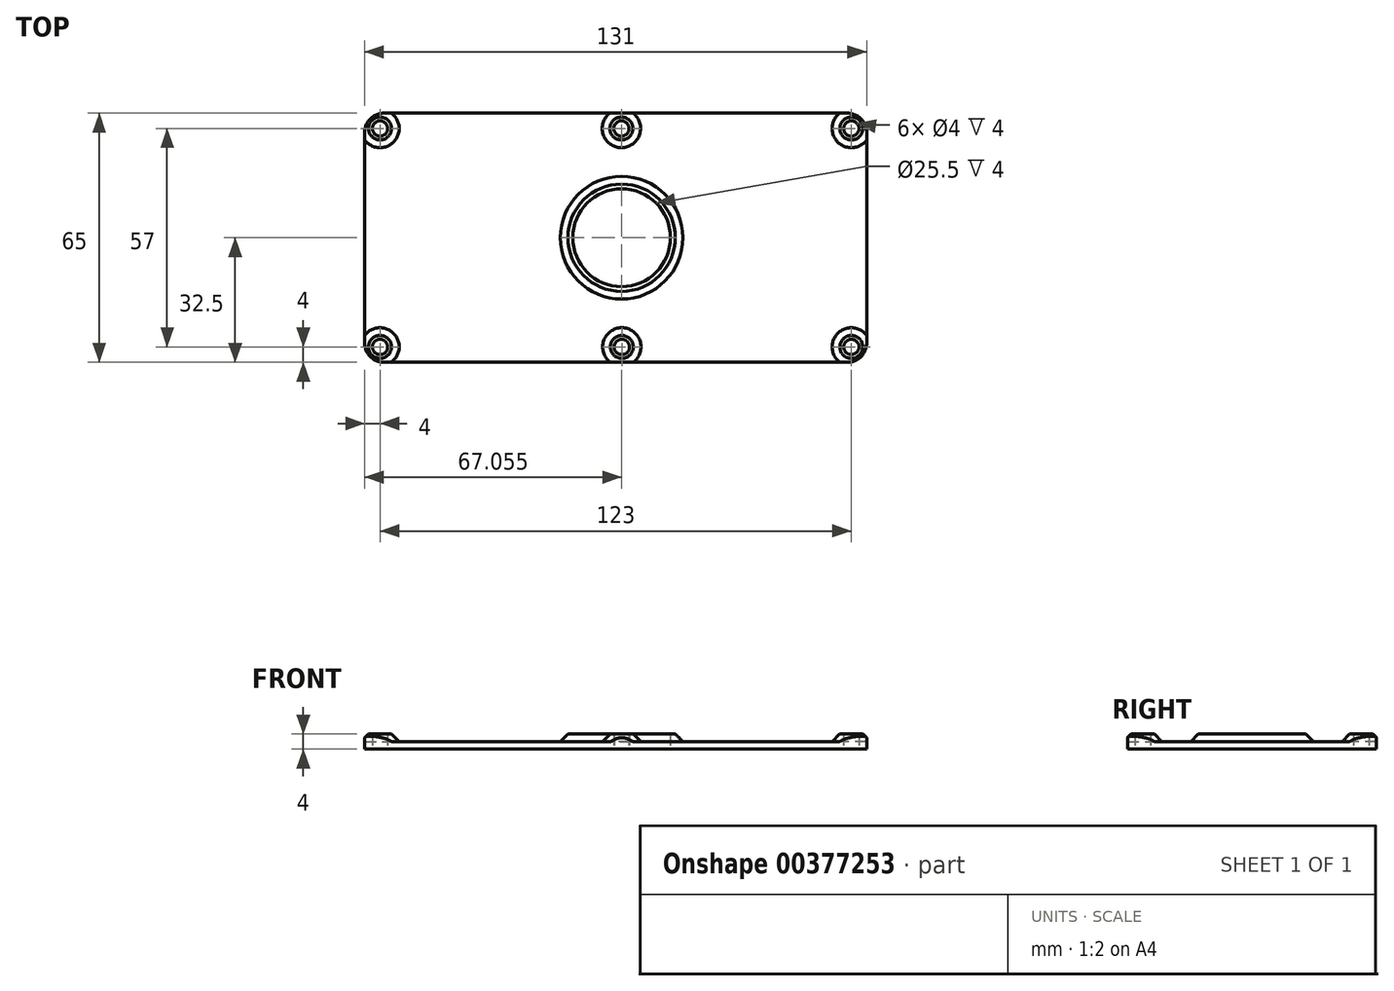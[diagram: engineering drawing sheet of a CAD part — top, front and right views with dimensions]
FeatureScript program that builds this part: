
annotation { "Feature Type Name" : "Feature", "Feature Type Description" : "" }
export const myFeature = defineFeature(function(context is Context, id is Id, definition is map)
    precondition{}
    {
        {
            var Q0;
            Q0=qCreatedBy(makeId("Top.planeOp"),FACE);
            var sketch = newSketch(context, id + "F0", { "sketchPlane" : qUnion([Q0])});
            skLineSegment(sketch, "E0.bottom", {"start": v(-65.5, 32.5) * mm, "end": v(65.5, 32.5) * mm});
            skLineSegment(sketch, "E0.top", {"start": v(-65.5, -32.5) * mm, "end": v(65.5, -32.5) * mm});
            skLineSegment(sketch, "E0.left", {"start": v(-65.5, 32.5) * mm, "end": v(-65.5, -32.5) * mm});
            skLineSegment(sketch, "E0.right", {"start": v(65.5, 32.5) * mm, "end": v(65.5, -32.5) * mm});
            skPoint(sketch, "E0.middle", {"position": v(0, 0) * mm});
            skLineSegment(sketch, "E1.bottom", {"start": v(-65.5, 32.5) * mm, "end": v(-61.5, 32.5) * mm, "construction": true});
            skLineSegment(sketch, "E1.top", {"start": v(-65.5, 28.5) * mm, "end": v(-61.5, 28.5) * mm, "construction": true});
            skLineSegment(sketch, "E1.left", {"start": v(-65.5, 32.5) * mm, "end": v(-65.5, 28.5) * mm, "construction": true});
            skLineSegment(sketch, "E1.right", {"start": v(-61.5, 32.5) * mm, "end": v(-61.5, 28.5) * mm, "construction": true});
            skLineSegment(sketch, "E2.bottom", {"start": v(65.5, 32.5) * mm, "end": v(61.5, 32.5) * mm, "construction": true});
            skLineSegment(sketch, "E2.top", {"start": v(65.5, 28.5) * mm, "end": v(61.5, 28.5) * mm, "construction": true});
            skLineSegment(sketch, "E2.left", {"start": v(65.5, 32.5) * mm, "end": v(65.5, 28.5) * mm, "construction": true});
            skLineSegment(sketch, "E2.right", {"start": v(61.5, 32.5) * mm, "end": v(61.5, 28.5) * mm, "construction": true});
            skLineSegment(sketch, "E3.bottom", {"start": v(-65.5, -32.5) * mm, "end": v(-61.5, -32.5) * mm, "construction": true});
            skLineSegment(sketch, "E3.top", {"start": v(-65.5, -28.5) * mm, "end": v(-61.5, -28.5) * mm, "construction": true});
            skLineSegment(sketch, "E3.left", {"start": v(-65.5, -32.5) * mm, "end": v(-65.5, -28.5) * mm, "construction": true});
            skLineSegment(sketch, "E3.right", {"start": v(-61.5, -32.5) * mm, "end": v(-61.5, -28.5) * mm, "construction": true});
            skLineSegment(sketch, "E4.bottom", {"start": v(65.5, -32.5) * mm, "end": v(61.5, -32.5) * mm, "construction": true});
            skLineSegment(sketch, "E4.top", {"start": v(65.5, -28.5) * mm, "end": v(61.5, -28.5) * mm, "construction": true});
            skLineSegment(sketch, "E4.left", {"start": v(65.5, -32.5) * mm, "end": v(65.5, -28.5) * mm, "construction": true});
            skLineSegment(sketch, "E4.right", {"start": v(61.5, -32.5) * mm, "end": v(61.5, -28.5) * mm, "construction": true});
            skCircle(sketch, "E5", {"center": v(-61.5, 28.5) * mm, "radius": 3 * mm});
            skCircle(sketch, "E6", {"center": v(-61.5, -28.5) * mm, "radius": 3 * mm});
            skCircle(sketch, "E7", {"center": v(61.5, -28.5) * mm, "radius": 3 * mm});
            skCircle(sketch, "E8", {"center": v(61.5, 28.5) * mm, "radius": 3 * mm});
            skLineSegment(sketch, "E9", {"start": v(65.5, 28.5) * mm, "end": v(1.5, 28.5) * mm, "construction": true});
            skPoint(sketch, "E9.endSnap0", {"position": v(63.5, 28.5) * mm});
            skLineSegment(sketch, "E10", {"start": v(65.5, -28.5) * mm, "end": v(1.61, -28.5) * mm});
            skLineSegment(sketch, "E11", {"start": v(1.5, 28.5) * mm, "end": v(1.5, 32.5) * mm, "construction": true});
            skLineSegment(sketch, "E12", {"start": v(1.61, -28.5) * mm, "end": v(1.61, -32.5) * mm, "construction": true});
            skCircle(sketch, "E13", {"center": v(1.5, 28.5) * mm, "radius": 3 * mm});
            skCircle(sketch, "E14", {"center": v(1.61, -28.5) * mm, "radius": 3 * mm});
            skLineSegment(sketch, "E15", {"start": v(1.5, 28.5) * mm, "end": v(1.61, -29.33) * mm, "construction": true});
            skCircle(sketch, "E16", {"center": v(1.55, 0) * mm, "radius": 14 * mm});
            skCircle(sketch, "E17", {"center": v(1.55, 0) * mm, "radius": 12.75 * mm});
            skSolve(sketch);
        }
        {
            var Q0;
            {var subQ7=sQuery(id+"F0.wireOp",EDGE,"E0.bottom");Q0=makeQuery(id+"F0.imprint","IMPRINT",FACE,{"disambiguationData":[TD([[makeQuery(id+"F0.imprint","IMPRINT",EDGE,{"derivedFrom":subQ7}),-1.0]])]});}
            var Q1;
            Q1=makeQuery(id+"F0.imprint","IMPRINT",FACE,{"disambiguationData":[TD([[makeQuery(id+"F0.imprint","IMPRINT",EDGE,{"derivedFrom":sQuery(id+"F0.wireOp",EDGE,"E13")}),1.0]])]});
            var Q2;
            Q2=makeQuery(id+"F0.imprint","IMPRINT",FACE,{"disambiguationData":[TD([[makeQuery(id+"F0.imprint","IMPRINT",EDGE,{"derivedFrom":sQuery(id+"F0.wireOp",EDGE,"E14")}),1.0]])]});
            var Q3;
            {var subQ0=sQuery(id+"F0.wireOp",EDGE,"E10");var subQ1=sQuery(id+"F0.wireOp",EDGE,"E7");var subQ2=makeQuery(id+"F0.imprint","INTERSECT",VERTEX,{"disambiguationData":[OD(0.0)],"derivedFrom":[subQ1,subQ0]});Q3=makeQuery(id+"F0.imprint","IMPRINT",FACE,{"disambiguationData":[TD([[makeQuery(id+"F0.imprint","IMPRINT",EDGE,{"disambiguationData":[TD([[subQ2,1.0]])],"derivedFrom":subQ1}),1.0]])]});}
            var Q4;
            {var subQ0=sQuery(id+"F0.wireOp",EDGE,"E10");var subQ1=sQuery(id+"F0.wireOp",EDGE,"E7");var subQ2=makeQuery(id+"F0.imprint","INTERSECT",VERTEX,{"disambiguationData":[OD(0.0)],"derivedFrom":[subQ1,subQ0]});Q4=makeQuery(id+"F0.imprint","IMPRINT",FACE,{"disambiguationData":[TD([[makeQuery(id+"F0.imprint","IMPRINT",EDGE,{"disambiguationData":[TD([[subQ2,-1.0]])],"derivedFrom":subQ1}),1.0]])]});}
            var Q5;
            Q5=makeQuery(id+"F0.imprint","IMPRINT",FACE,{"disambiguationData":[TD([[makeQuery(id+"F0.imprint","IMPRINT",EDGE,{"derivedFrom":sQuery(id+"F0.wireOp",EDGE,"E8")}),1.0]])]});
            var Q6;
            Q6=makeQuery(id+"F0.imprint","IMPRINT",FACE,{"disambiguationData":[TD([[makeQuery(id+"F0.imprint","IMPRINT",EDGE,{"derivedFrom":sQuery(id+"F0.wireOp",EDGE,"E6")}),1.0]])]});
            var Q7;
            Q7=makeQuery(id+"F0.imprint","IMPRINT",FACE,{"disambiguationData":[TD([[makeQuery(id+"F0.imprint","IMPRINT",EDGE,{"derivedFrom":sQuery(id+"F0.wireOp",EDGE,"E5")}),1.0]])]});
            var Q8;
            Q8=makeQuery(id+"F0.imprint","IMPRINT",FACE,{"disambiguationData":[TD([[makeQuery(id+"F0.imprint","IMPRINT",EDGE,{"derivedFrom":sQuery(id+"F0.wireOp",EDGE,"E16")}),1.0]])]});
            extrude(context, id + "F1", {"entities" : qUnion([Q0, Q1, Q2, Q3, Q4, Q5, Q6, Q7, Q8]), "depth" : 2 * mm});
        }
        {
            var Q0;
            Q0=makeQuery(id+"F0.imprint","IMPRINT",FACE,{"disambiguationData":[TD([[makeQuery(id+"F0.imprint","IMPRINT",EDGE,{"derivedFrom":sQuery(id+"F0.wireOp",EDGE,"E5")}),1.0]])]});
            var Q1;
            Q1=makeQuery(id+"F0.imprint","IMPRINT",FACE,{"disambiguationData":[TD([[makeQuery(id+"F0.imprint","IMPRINT",EDGE,{"derivedFrom":sQuery(id+"F0.wireOp",EDGE,"E6")}),1.0]])]});
            var Q2;
            Q2=makeQuery(id+"F0.imprint","IMPRINT",FACE,{"disambiguationData":[TD([[makeQuery(id+"F0.imprint","IMPRINT",EDGE,{"derivedFrom":sQuery(id+"F0.wireOp",EDGE,"E14")}),1.0]])]});
            var Q3;
            {var subQ0=sQuery(id+"F0.wireOp",EDGE,"E10");var subQ1=sQuery(id+"F0.wireOp",EDGE,"E7");var subQ2=makeQuery(id+"F0.imprint","INTERSECT",VERTEX,{"disambiguationData":[OD(0.0)],"derivedFrom":[subQ1,subQ0]});Q3=makeQuery(id+"F0.imprint","IMPRINT",FACE,{"disambiguationData":[TD([[makeQuery(id+"F0.imprint","IMPRINT",EDGE,{"disambiguationData":[TD([[subQ2,1.0]])],"derivedFrom":subQ1}),1.0]])]});}
            var Q4;
            {var subQ0=sQuery(id+"F0.wireOp",EDGE,"E10");var subQ1=sQuery(id+"F0.wireOp",EDGE,"E7");var subQ2=makeQuery(id+"F0.imprint","INTERSECT",VERTEX,{"disambiguationData":[OD(0.0)],"derivedFrom":[subQ1,subQ0]});Q4=makeQuery(id+"F0.imprint","IMPRINT",FACE,{"disambiguationData":[TD([[makeQuery(id+"F0.imprint","IMPRINT",EDGE,{"disambiguationData":[TD([[subQ2,-1.0]])],"derivedFrom":subQ1}),1.0]])]});}
            var Q5;
            Q5=makeQuery(id+"F0.imprint","IMPRINT",FACE,{"disambiguationData":[TD([[makeQuery(id+"F0.imprint","IMPRINT",EDGE,{"derivedFrom":sQuery(id+"F0.wireOp",EDGE,"E8")}),1.0]])]});
            var Q6;
            Q6=makeQuery(id+"F0.imprint","IMPRINT",FACE,{"disambiguationData":[TD([[makeQuery(id+"F0.imprint","IMPRINT",EDGE,{"derivedFrom":sQuery(id+"F0.wireOp",EDGE,"E13")}),1.0]])]});
            extrude(context, id + "F2", {"entities" : qUnion([Q0, Q1, Q2, Q3, Q4, Q5, Q6]), "operationType" : NewBodyOperationType.ADD, "depth" : 4 * mm});
        }
        {
            var Q0;
            Q0=makeQuery(id+"F2.opExtrude","CAP_FACE",FACE,{"disambiguationData":[OSD([sQuery(id+"F0.wireOp",EDGE,"E5")])],"isStart":false});
            var Q1;
            Q1=makeQuery(id+"F2.opExtrude","CAP_FACE",FACE,{"disambiguationData":[OSD([sQuery(id+"F0.wireOp",EDGE,"E13")])],"isStart":false});
            var Q2;
            Q2=makeQuery(id+"F2.opExtrude","CAP_FACE",FACE,{"disambiguationData":[OSD([sQuery(id+"F0.wireOp",EDGE,"E8")])],"isStart":false});
            var Q3;
            Q3=makeQuery(id+"F2.opExtrude","CAP_FACE",FACE,{"disambiguationData":[OSD([sQuery(id+"F0.wireOp",EDGE,"E7")])],"isStart":false});
            var Q4;
            Q4=makeQuery(id+"F2.opExtrude","CAP_FACE",FACE,{"disambiguationData":[OSD([sQuery(id+"F0.wireOp",EDGE,"E14")])],"isStart":false});
            var Q5;
            Q5=makeQuery(id+"F2.opExtrude","CAP_FACE",FACE,{"disambiguationData":[OSD([sQuery(id+"F0.wireOp",EDGE,"E6")])],"isStart":false});
            shell(context, id + "F3", {"entities" : qUnion([Q0, Q1, Q2, Q3, Q4, Q5]), "thickness" : 1 * mm});
        }
        {
            var Q0;
            Q0=makeQuery(id+"F0.imprint","IMPRINT",FACE,{"disambiguationData":[TD([[makeQuery(id+"F0.imprint","IMPRINT",EDGE,{"derivedFrom":sQuery(id+"F0.wireOp",EDGE,"E16")}),1.0]])]});
            extrude(context, id + "F4", {"entities" : qUnion([Q0]), "operationType" : NewBodyOperationType.ADD, "depth" : 4 * mm});
        }
        {
            var Q0;
            Q0=makeQuery(id+"F1.opExtrude","SWEPT_EDGE",EDGE,{"disambiguationData":[OSD([sQuery(id+"F0.wireOp",EDGE,"E0.top"),sQuery(id+"F0.wireOp",EDGE,"E0.right")])]});
            var Q1;
            Q1=makeQuery(id+"F1.opExtrude","SWEPT_EDGE",EDGE,{"disambiguationData":[OSD([sQuery(id+"F0.wireOp",EDGE,"E0.top"),sQuery(id+"F0.wireOp",EDGE,"E0.left")])]});
            var Q2;
            Q2=makeQuery(id+"F1.opExtrude","SWEPT_EDGE",EDGE,{"disambiguationData":[OSD([sQuery(id+"F0.wireOp",EDGE,"E0.bottom"),sQuery(id+"F0.wireOp",EDGE,"E0.right")])]});
            var Q3;
            Q3=makeQuery(id+"F1.opExtrude","SWEPT_EDGE",EDGE,{"disambiguationData":[OSD([sQuery(id+"F0.wireOp",EDGE,"E0.bottom"),sQuery(id+"F0.wireOp",EDGE,"E0.left")])]});
            fillet(context, id + "F5", {"entities" : qUnion([Q0, Q1, Q2, Q3]), "radius" : 5 * mm, "tangentPropagation" : true, "allowEdgeOverflow" : false});
        }
        {
            var Q0;
            Q0=makeQuery(id+"F4.boolean.opBoolean","INTERSECT",EDGE,{"derivedFrom":[makeQuery(id+"F1.opExtrude","CAP_FACE",FACE,{"disambiguationData":[OSD([sQuery(id+"F0.wireOp",EDGE,"E0.bottom"),sQuery(id+"F0.wireOp",EDGE,"E0.top"),sQuery(id+"F0.wireOp",EDGE,"E0.left"),sQuery(id+"F0.wireOp",EDGE,"E0.right"),sQuery(id+"F0.wireOp",EDGE,"E17")])],"isStart":false}),makeQuery(id+"F4.opExtrude","SWEPT_FACE",FACE,{"disambiguationData":[OSD([sQuery(id+"F0.wireOp",EDGE,"E16")])]})]});
            var Q1;
            Q1=makeQuery(id+"F2.boolean.opBoolean","INTERSECT",EDGE,{"derivedFrom":[makeQuery(id+"F1.opExtrude","CAP_FACE",FACE,{"disambiguationData":[OSD([sQuery(id+"F0.wireOp",EDGE,"E0.bottom"),sQuery(id+"F0.wireOp",EDGE,"E0.top"),sQuery(id+"F0.wireOp",EDGE,"E0.left"),sQuery(id+"F0.wireOp",EDGE,"E0.right"),sQuery(id+"F0.wireOp",EDGE,"E17")])],"isStart":false}),makeQuery(id+"F2.opExtrude","SWEPT_FACE",FACE,{"disambiguationData":[OSD([sQuery(id+"F0.wireOp",EDGE,"E14")])]})]});
            var Q2;
            Q2=makeQuery(id+"F2.boolean.opBoolean","INTERSECT",EDGE,{"derivedFrom":[makeQuery(id+"F1.opExtrude","CAP_FACE",FACE,{"disambiguationData":[OSD([sQuery(id+"F0.wireOp",EDGE,"E0.bottom"),sQuery(id+"F0.wireOp",EDGE,"E0.top"),sQuery(id+"F0.wireOp",EDGE,"E0.left"),sQuery(id+"F0.wireOp",EDGE,"E0.right"),sQuery(id+"F0.wireOp",EDGE,"E17")])],"isStart":false}),makeQuery(id+"F2.opExtrude","SWEPT_FACE",FACE,{"disambiguationData":[OSD([sQuery(id+"F0.wireOp",EDGE,"E6")])]})]});
            var Q3;
            Q3=makeQuery(id+"F2.boolean.opBoolean","INTERSECT",EDGE,{"derivedFrom":[makeQuery(id+"F1.opExtrude","CAP_FACE",FACE,{"disambiguationData":[OSD([sQuery(id+"F0.wireOp",EDGE,"E0.bottom"),sQuery(id+"F0.wireOp",EDGE,"E0.top"),sQuery(id+"F0.wireOp",EDGE,"E0.left"),sQuery(id+"F0.wireOp",EDGE,"E0.right"),sQuery(id+"F0.wireOp",EDGE,"E17")])],"isStart":false}),makeQuery(id+"F2.opExtrude","SWEPT_FACE",FACE,{"disambiguationData":[OSD([sQuery(id+"F0.wireOp",EDGE,"E7")])]})]});
            var Q4;
            Q4=makeQuery(id+"F2.boolean.opBoolean","INTERSECT",EDGE,{"derivedFrom":[makeQuery(id+"F1.opExtrude","CAP_FACE",FACE,{"disambiguationData":[OSD([sQuery(id+"F0.wireOp",EDGE,"E0.bottom"),sQuery(id+"F0.wireOp",EDGE,"E0.top"),sQuery(id+"F0.wireOp",EDGE,"E0.left"),sQuery(id+"F0.wireOp",EDGE,"E0.right"),sQuery(id+"F0.wireOp",EDGE,"E17")])],"isStart":false}),makeQuery(id+"F2.opExtrude","SWEPT_FACE",FACE,{"disambiguationData":[OSD([sQuery(id+"F0.wireOp",EDGE,"E8")])]})]});
            var Q5;
            Q5=makeQuery(id+"F2.boolean.opBoolean","INTERSECT",EDGE,{"derivedFrom":[makeQuery(id+"F1.opExtrude","CAP_FACE",FACE,{"disambiguationData":[OSD([sQuery(id+"F0.wireOp",EDGE,"E0.bottom"),sQuery(id+"F0.wireOp",EDGE,"E0.top"),sQuery(id+"F0.wireOp",EDGE,"E0.left"),sQuery(id+"F0.wireOp",EDGE,"E0.right"),sQuery(id+"F0.wireOp",EDGE,"E17")])],"isStart":false}),makeQuery(id+"F2.opExtrude","SWEPT_FACE",FACE,{"disambiguationData":[OSD([sQuery(id+"F0.wireOp",EDGE,"E13")])]})]});
            var Q6;
            Q6=makeQuery(id+"F2.boolean.opBoolean","INTERSECT",EDGE,{"derivedFrom":[makeQuery(id+"F1.opExtrude","CAP_FACE",FACE,{"disambiguationData":[OSD([sQuery(id+"F0.wireOp",EDGE,"E0.bottom"),sQuery(id+"F0.wireOp",EDGE,"E0.top"),sQuery(id+"F0.wireOp",EDGE,"E0.left"),sQuery(id+"F0.wireOp",EDGE,"E0.right"),sQuery(id+"F0.wireOp",EDGE,"E17")])],"isStart":false}),makeQuery(id+"F2.opExtrude","SWEPT_FACE",FACE,{"disambiguationData":[OSD([sQuery(id+"F0.wireOp",EDGE,"E5")])]})]});
            chamfer(context, id + "F6", {"entities" : qUnion([Q0, Q1, Q2, Q3, Q4, Q5, Q6]), "width" : 2 * mm, "tangentPropagation" : true});
        }
        {
            var Q0;
            Q0=makeQuery(id+"F3.opShell","OFFSET_FACE",FACE,{"disambiguationData":[OSD([sQuery(id+"F0.wireOp",EDGE,"E0.bottom"),sQuery(id+"F0.wireOp",EDGE,"E0.top"),sQuery(id+"F0.wireOp",EDGE,"E0.left"),sQuery(id+"F0.wireOp",EDGE,"E0.right"),sQuery(id+"F0.wireOp",EDGE,"E17")]),OD(0.0)]});
            var Q1;
            Q1=makeQuery(id+"F3.opShell","OFFSET_FACE",FACE,{"disambiguationData":[OSD([sQuery(id+"F0.wireOp",EDGE,"E0.bottom"),sQuery(id+"F0.wireOp",EDGE,"E0.top"),sQuery(id+"F0.wireOp",EDGE,"E0.left"),sQuery(id+"F0.wireOp",EDGE,"E0.right"),sQuery(id+"F0.wireOp",EDGE,"E17")]),OD(4.0)]});
            var Q2;
            Q2=makeQuery(id+"F3.opShell","OFFSET_FACE",FACE,{"disambiguationData":[OSD([sQuery(id+"F0.wireOp",EDGE,"E0.bottom"),sQuery(id+"F0.wireOp",EDGE,"E0.top"),sQuery(id+"F0.wireOp",EDGE,"E0.left"),sQuery(id+"F0.wireOp",EDGE,"E0.right"),sQuery(id+"F0.wireOp",EDGE,"E17")]),OD(3.0)]});
            var Q3;
            Q3=makeQuery(id+"F3.opShell","OFFSET_FACE",FACE,{"disambiguationData":[OSD([sQuery(id+"F0.wireOp",EDGE,"E0.bottom"),sQuery(id+"F0.wireOp",EDGE,"E0.top"),sQuery(id+"F0.wireOp",EDGE,"E0.left"),sQuery(id+"F0.wireOp",EDGE,"E0.right"),sQuery(id+"F0.wireOp",EDGE,"E17")]),OD(2.0)]});
            var Q4;
            Q4=makeQuery(id+"F3.opShell","OFFSET_FACE",FACE,{"disambiguationData":[OSD([sQuery(id+"F0.wireOp",EDGE,"E0.bottom"),sQuery(id+"F0.wireOp",EDGE,"E0.top"),sQuery(id+"F0.wireOp",EDGE,"E0.left"),sQuery(id+"F0.wireOp",EDGE,"E0.right"),sQuery(id+"F0.wireOp",EDGE,"E17")]),OD(5.0)]});
            var Q5;
            Q5=makeQuery(id+"F3.opShell","OFFSET_FACE",FACE,{"disambiguationData":[OSD([sQuery(id+"F0.wireOp",EDGE,"E0.bottom"),sQuery(id+"F0.wireOp",EDGE,"E0.top"),sQuery(id+"F0.wireOp",EDGE,"E0.left"),sQuery(id+"F0.wireOp",EDGE,"E0.right"),sQuery(id+"F0.wireOp",EDGE,"E17")]),OD(1.0)]});
            extrude(context, id + "F7", {"entities" : qUnion([Q0, Q1, Q2, Q3, Q4, Q5]), "operationType" : NewBodyOperationType.REMOVE, "oppositeDirection" : true, "depth" : 25 * mm});
        }
    });
